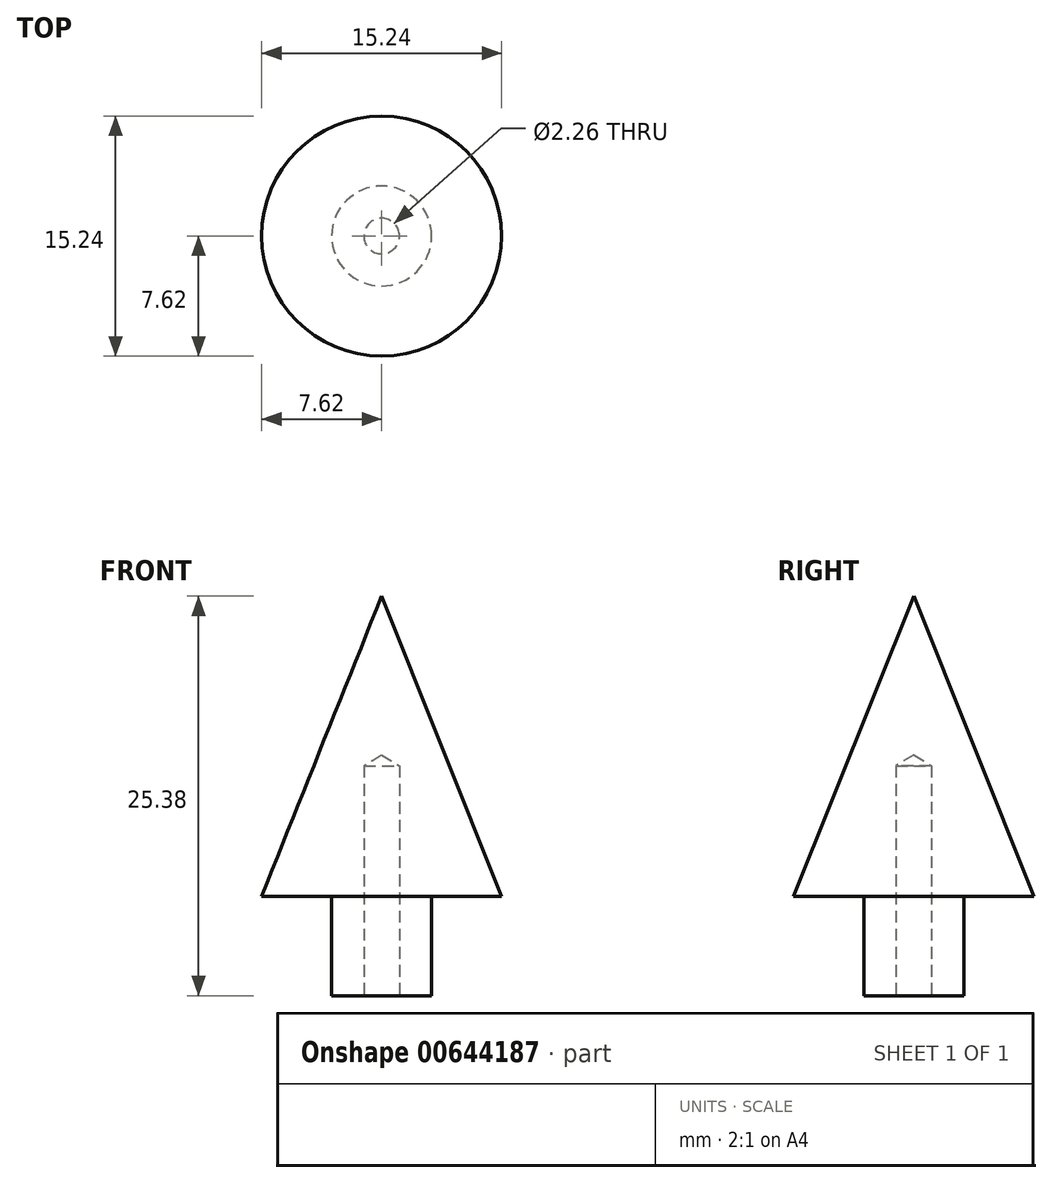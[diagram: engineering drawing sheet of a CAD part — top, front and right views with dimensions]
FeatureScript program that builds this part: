
annotation { "Feature Type Name" : "Feature", "Feature Type Description" : "" }
export const myFeature = defineFeature(function(context is Context, id is Id, definition is map)
    precondition{}
    {
        {
            var Q0;
            Q0=qCreatedBy(makeId("Front.planeOp"),FACE);
            var sketch = newSketch(context, id + "F0", { "sketchPlane" : qUnion([Q0])});
            skLineSegment(sketch, "E0.bottom", {"start": v(0, 0) * mm, "end": v(-3.17, 0) * mm});
            skLineSegment(sketch, "E0.top", {"start": v(0, -6.32) * mm, "end": v(-3.17, -6.32) * mm});
            skLineSegment(sketch, "E0.left", {"start": v(0, 0) * mm, "end": v(0, -6.32) * mm});
            skLineSegment(sketch, "E0.right", {"start": v(-3.17, 0) * mm, "end": v(-3.17, -6.32) * mm});
            skLineSegment(sketch, "E1", {"start": v(-3.17, 0) * mm, "end": v(-7.62, 0) * mm});
            skLineSegment(sketch, "E2", {"start": v(0, 0) * mm, "end": v(0, 19.06) * mm});
            skLineSegment(sketch, "E3", {"start": v(0, 19.06) * mm, "end": v(-7.62, 0) * mm});
            skSolve(sketch);
        }
        {
            var Q0;
            Q0 = qSketchRegion(id + "F0", true);
            var Q1;
            Q1=sQuery(id+"F0.wireOp",EDGE,"E2");
            revolve(context, id + "F1", {"entities" : qUnion([Q0]), "axis" : qUnion([Q1]), "revolveType" : RevolveType.FULL});
        }
        {
            var Q0;
            Q0=makeQuery(id+"F1.opRevolve","SWEPT_FACE",FACE,{"disambiguationData":[OSD([sQuery(id+"F0.wireOp",EDGE,"E0.top")])]});
            var sketch = newSketch(context, id + "F2", { "sketchPlane" : qUnion([Q0])});
            skPoint(sketch, "E4", {"position": v(0, 0) * mm});
            skSolve(sketch);
        }
        {
            var Q0;
            Q0=sQuery(id+"F2.wireOp",VERTEX,"E4");
            var Q1;
            Q1=makeQuery(id+"F1.opRevolve","SWEPT_BODY",BODY,{"disambiguationData":[OSD([sQuery(id+"F0.wireOp",EDGE,"E0.top"),sQuery(id+"F0.wireOp",EDGE,"E0.left"),sQuery(id+"F0.wireOp",EDGE,"E0.right"),sQuery(id+"F0.wireOp",EDGE,"E1"),sQuery(id+"F0.wireOp",EDGE,"E2"),sQuery(id+"F0.wireOp",EDGE,"E3")])]});
            hole(context, id + "F3", {"style" : HoleStyle.SIMPLE, "endStyle" : HoleEndStyle.BLIND, "standardTappedOrClearance" : lookupTablePath({ "standard" : "ANSI", "engagement" : "75%", "pitch" : "40 tpi", "size" : "#4", "type" : "Tapped" }), "standardBlindInLast" : lookupTablePath({ "standard" : "ANSI", "engagement" : "75%", "pitch" : "40 tpi", "size" : "#4", "type" : "Tapped" }), "holeDiameter" : 2.26 * mm, "majorDiameter" : 2.84 * mm, "showTappedDepth" : true, "holeDepth" : 14.6 * mm, "isTappedThrough" : true, "tappedDepth" : 12.7 * mm, "tapClearance" : 3, "locations" : qUnion([Q0]), "scope" : qUnion([Q1])});
        }
    });
